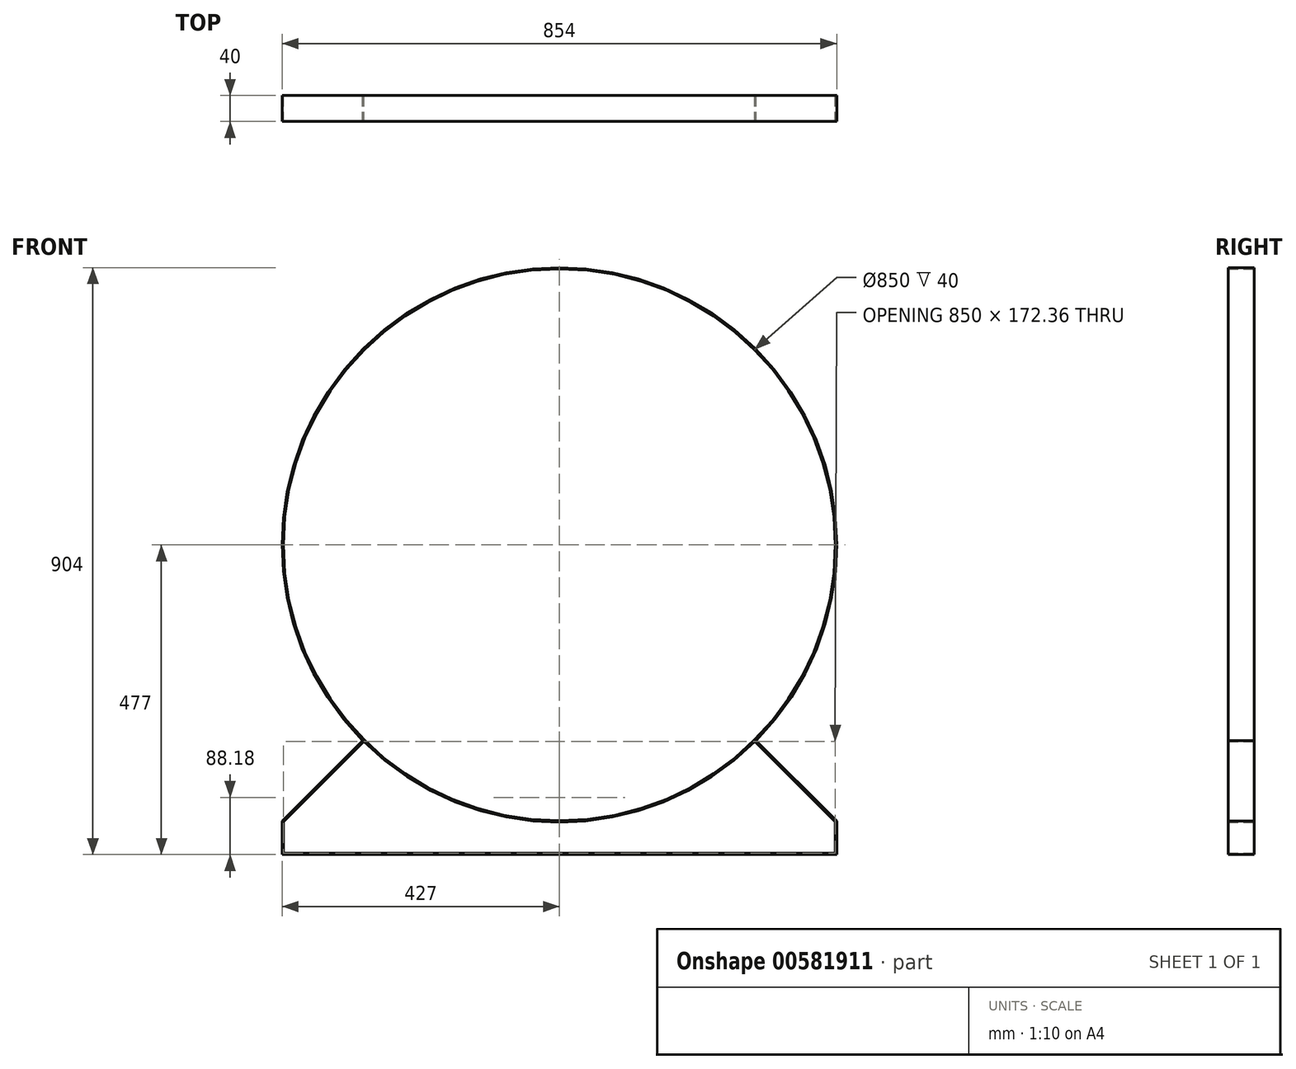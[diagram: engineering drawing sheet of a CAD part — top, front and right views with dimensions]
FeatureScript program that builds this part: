
annotation { "Feature Type Name" : "Feature", "Feature Type Description" : "" }
export const myFeature = defineFeature(function(context is Context, id is Id, definition is map)
    precondition{}
    {
        {
            var Q0;
            Q0=qCreatedBy(makeId("Front.planeOp"),FACE);
            var sketch = newSketch(context, id + "F0", { "sketchPlane" : qUnion([Q0])});
            skLineSegment(sketch, "E0", {"start": v(0, 0) * mm, "end": v(-679.96, 0) * mm, "construction": true});
            skLineSegment(sketch, "E1", {"start": v(0, 0) * mm, "end": v(0, 658.78) * mm, "construction": true});
            skLineSegment(sketch, "E2", {"start": v(0, 0) * mm, "end": v(-291.77, -291.77) * mm, "construction": true});
            skLineSegment(sketch, "E3", {"start": v(0, 0) * mm, "end": v(291.77, -291.77) * mm, "construction": true});
            skCircle(sketch, "E4", {"center": v(0, 0) * mm, "radius": 425 * mm});
            skCircle(sketch, "E5", {"center": v(0, 0) * mm, "radius": 427 * mm});
            skLineSegment(sketch, "E6", {"start": v(-427, -477) * mm, "end": v(0, -477) * mm});
            skLineSegment(sketch, "E7", {"start": v(-425, -475) * mm, "end": v(0, -475) * mm});
            skLineSegment(sketch, "E8", {"start": v(0, 0) * mm, "end": v(0, -311.11) * mm, "construction": true});
            skLineSegment(sketch, "E9", {"start": v(-425, -475) * mm, "end": v(-425, -426.41) * mm});
            skLineSegment(sketch, "E10", {"start": v(-427, -477) * mm, "end": v(-427, -425.59) * mm});
            skLineSegment(sketch, "E11", {"start": v(-302.64, -301.23) * mm, "end": v(-427, -425.59) * mm});
            skLineSegment(sketch, "E12", {"start": v(-301.23, -302.64) * mm, "end": v(-425, -426.41) * mm});
            skLineSegment(sketch, "E13.MirrorCS", {"start": v(301.23, -302.64) * mm, "end": v(425, -426.41) * mm});
            skLineSegment(sketch, "E14.MirrorCS", {"start": v(427, -477) * mm, "end": v(0, -477) * mm});
            skLineSegment(sketch, "E15.MirrorCS", {"start": v(425, -475) * mm, "end": v(0, -475) * mm});
            skLineSegment(sketch, "E16.MirrorCS", {"start": v(302.64, -301.23) * mm, "end": v(427, -425.59) * mm});
            skLineSegment(sketch, "E17.MirrorCS", {"start": v(425, -475) * mm, "end": v(425, -426.41) * mm});
            skLineSegment(sketch, "E18.MirrorCS", {"start": v(427, -477) * mm, "end": v(427, -425.59) * mm});
            skSolve(sketch);
        }
        {
            var Q0;
            Q0=qSketchRegion(id+"F0",true);
            extrude(context, id + "F1", {"entities" : qUnion([Q0]), "offsetDistance" : 25 * mm, "depth" : 40 * mm});
        }
    });
